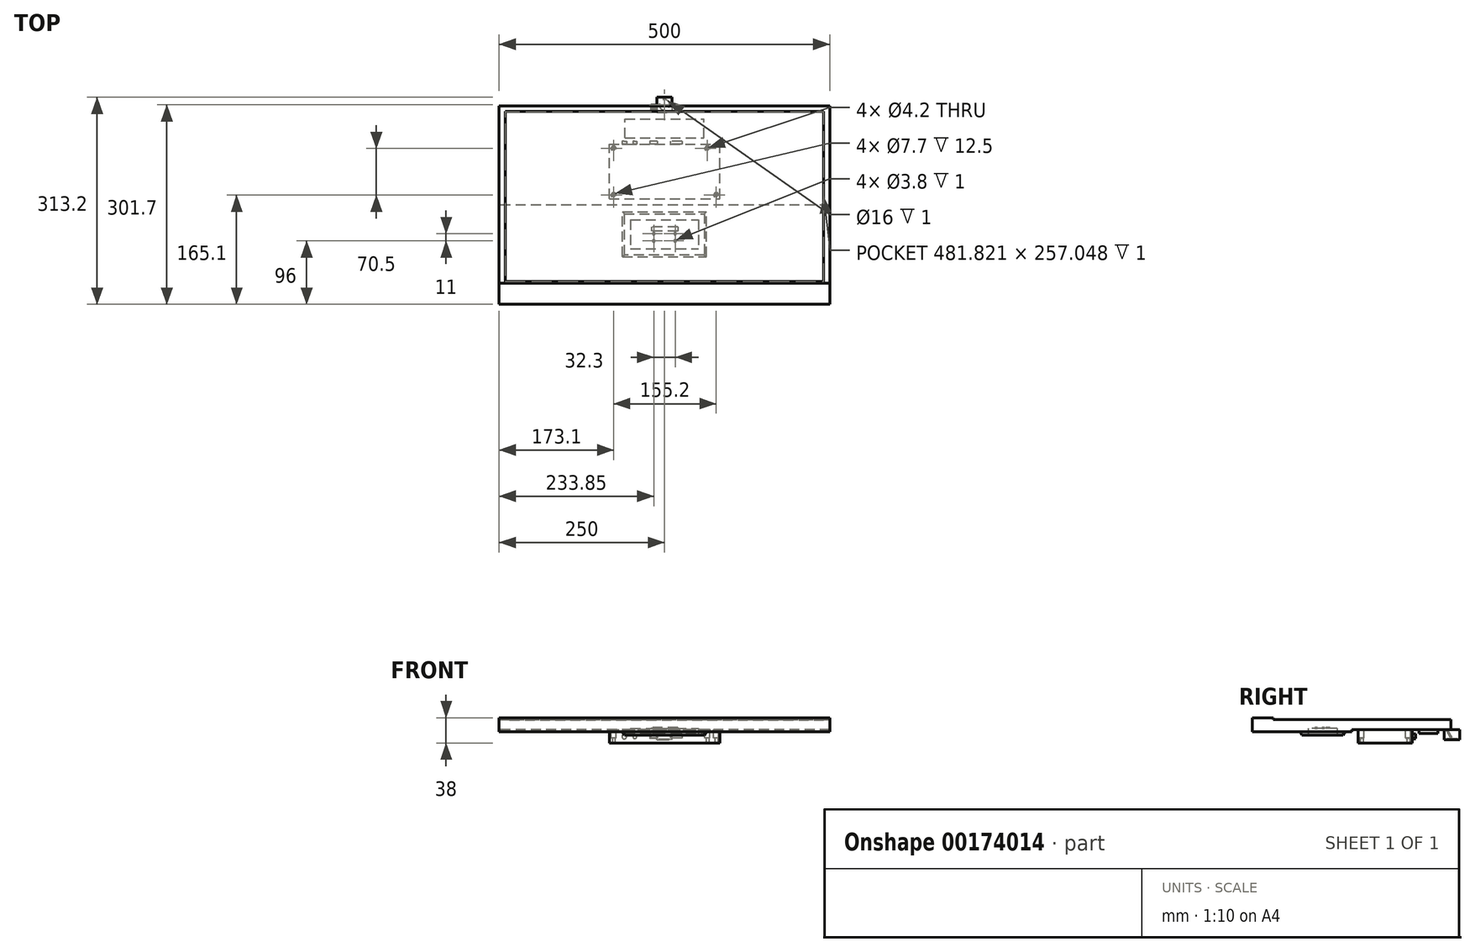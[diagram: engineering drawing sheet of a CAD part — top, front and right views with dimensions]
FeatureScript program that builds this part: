
annotation { "Feature Type Name" : "Feature", "Feature Type Description" : "" }
export const myFeature = defineFeature(function(context is Context, id is Id, definition is map)
    precondition{}
    {
        {
            var Q0;
            Q0=qCreatedBy(makeId("Top.planeOp"),FACE);
            var sketch = newSketch(context, id + "F0", { "sketchPlane" : qUnion([Q0])});
            skLineSegment(sketch, "E0.bottom", {"start": v(250, 150) * mm, "end": v(-250, 150) * mm});
            skLineSegment(sketch, "E0.top", {"start": v(250, -150) * mm, "end": v(-250, -150) * mm});
            skLineSegment(sketch, "E0.left", {"start": v(250, 150) * mm, "end": v(250, -150) * mm});
            skLineSegment(sketch, "E0.right", {"start": v(-250, 150) * mm, "end": v(-250, -150) * mm});
            skPoint(sketch, "E0.middle", {"position": v(0, 0) * mm});
            skSolve(sketch);
        }
        {
            var Q0;
            Q0 = qSketchRegion(id + "F0", true);
            extrude(context, id + "F1", {"entities" : qUnion([Q0]), "depth" : 15 * mm});
        }
        {
            var Q0;
            Q0=makeQuery(id+"F1.opExtrude","CAP_FACE",FACE,{"disambiguationData":[OSD([sQuery(id+"F0.wireOp",EDGE,"E0.bottom"),sQuery(id+"F0.wireOp",EDGE,"E0.top"),sQuery(id+"F0.wireOp",EDGE,"E0.left"),sQuery(id+"F0.wireOp",EDGE,"E0.right")])],"isStart":false});
            var sketch = newSketch(context, id + "F2", { "sketchPlane" : qUnion([Q0])});
            skLineSegment(sketch, "E1.bottom", {"start": v(240.91, 141.46) * mm, "end": v(-240.91, 141.46) * mm});
            skLineSegment(sketch, "E1.top", {"start": v(240.91, -115.59) * mm, "end": v(-240.91, -115.59) * mm});
            skLineSegment(sketch, "E1.left", {"start": v(240.91, 141.46) * mm, "end": v(240.91, -115.59) * mm});
            skLineSegment(sketch, "E1.right", {"start": v(-240.91, 141.46) * mm, "end": v(-240.91, -115.59) * mm});
            skPoint(sketch, "E1.middle", {"position": v(0, 12.94) * mm});
            skSolve(sketch);
        }
        {
            var Q0;
            Q0 = qSketchRegion(id + "F2", true);
            extrude(context, id + "F3", {"entities" : qUnion([Q0]), "operationType" : NewBodyOperationType.REMOVE, "oppositeDirection" : true, "depth" : 1 * mm});
        }
        {
            var Q0;
            Q0=makeQuery(id+"F1.opExtrude","CAP_FACE",FACE,{"disambiguationData":[OSD([sQuery(id+"F0.wireOp",EDGE,"E0.bottom"),sQuery(id+"F0.wireOp",EDGE,"E0.top"),sQuery(id+"F0.wireOp",EDGE,"E0.left"),sQuery(id+"F0.wireOp",EDGE,"E0.right")])],"isStart":true});
            var sketch = newSketch(context, id + "F4", { "sketchPlane" : qUnion([Q0])});
            skLineSegment(sketch, "E2.bottom", {"start": v(250, 150) * mm, "end": v(-250, 150) * mm});
            skLineSegment(sketch, "E2.top", {"start": v(250, 0) * mm, "end": v(-250, 0) * mm});
            skLineSegment(sketch, "E2.left", {"start": v(250, 150) * mm, "end": v(250, 0) * mm});
            skLineSegment(sketch, "E2.right", {"start": v(-250, 150) * mm, "end": v(-250, 0) * mm});
            skSolve(sketch);
        }
        {
            var Q0;
            Q0 = qSketchRegion(id + "F4", true);
            extrude(context, id + "F5", {"entities" : qUnion([Q0]), "operationType" : NewBodyOperationType.ADD, "depth" : 3 * mm});
        }
        {
            var Q0;
            Q0=makeQuery(id+"F5.opExtrude","CAP_FACE",FACE,{"disambiguationData":[OSD([sQuery(id+"F4.wireOp",EDGE,"E2.bottom"),sQuery(id+"F4.wireOp",EDGE,"E2.top"),sQuery(id+"F4.wireOp",EDGE,"E2.left"),sQuery(id+"F4.wireOp",EDGE,"E2.right")])],"isStart":false});
            var sketch = newSketch(context, id + "F6", { "sketchPlane" : qUnion([Q0])});
            skLineSegment(sketch, "E3.bottom", {"start": v(-63.5, 78) * mm, "end": v(63.5, 78) * mm});
            skLineSegment(sketch, "E3.top", {"start": v(-63.5, 10) * mm, "end": v(63.5, 10) * mm});
            skLineSegment(sketch, "E3.left", {"start": v(-63.5, 78) * mm, "end": v(-63.5, 10) * mm});
            skLineSegment(sketch, "E3.right", {"start": v(63.5, 78) * mm, "end": v(63.5, 10) * mm});
            skPoint(sketch, "E3.middle", {"position": v(0, 44) * mm});
            skSolve(sketch);
        }
        {
            var Q0;
            Q0 = qSketchRegion(id + "F6", true);
            extrude(context, id + "F7", {"entities" : qUnion([Q0]), "operationType" : NewBodyOperationType.ADD, "depth" : 5 * mm});
        }
        {
            var Q0;
            Q0=makeQuery(id+"F7.opExtrude","CAP_FACE",FACE,{"disambiguationData":[OSD([sQuery(id+"F6.wireOp",EDGE,"E3.bottom"),sQuery(id+"F6.wireOp",EDGE,"E3.top"),sQuery(id+"F6.wireOp",EDGE,"E3.left"),sQuery(id+"F6.wireOp",EDGE,"E3.right")])],"isStart":false});
            chamfer(context, id + "F8", {"entities" : qUnion([Q0]), "chamferType" : ChamferType.OFFSET_ANGLE, "width" : 5 * mm, "oppositeDirection" : false, "angle" : 30 * degree, "tangentPropagation" : true});
        }
        {
            var Q0;
            Q0=makeQuery(id+"F7.opExtrude","CAP_FACE",FACE,{"disambiguationData":[OSD([sQuery(id+"F6.wireOp",EDGE,"E3.bottom"),sQuery(id+"F6.wireOp",EDGE,"E3.top"),sQuery(id+"F6.wireOp",EDGE,"E3.left"),sQuery(id+"F6.wireOp",EDGE,"E3.right")])],"isStart":false});
            var sketch = newSketch(context, id + "F9", { "sketchPlane" : qUnion([Q0])});
            skLineSegment(sketch, "E4.bottom", {"start": v(-51.3, 22) * mm, "end": v(51.3, 22) * mm});
            skLineSegment(sketch, "E4.top", {"start": v(-51.3, 66) * mm, "end": v(51.3, 66) * mm});
            skLineSegment(sketch, "E4.left", {"start": v(-51.3, 22) * mm, "end": v(-51.3, 66) * mm});
            skLineSegment(sketch, "E4.right", {"start": v(51.3, 22) * mm, "end": v(51.3, 66) * mm});
            skPoint(sketch, "E4.middle", {"position": v(0, 44) * mm});
            skPoint(sketch, "E4.middle.positionSnap0", {"position": v(60.61, 44) * mm});
            skPoint(sketch, "E4.middle.positionSnap1", {"position": v(0, 12.89) * mm});
            skPoint(sketch, "E4.centerSnap0", {"position": v(60.61, 44) * mm});
            skPoint(sketch, "E4.centerSnap1", {"position": v(0, 12.89) * mm});
            skSolve(sketch);
        }
        {
            var Q0;
            Q0 = qSketchRegion(id + "F9", true);
            extrude(context, id + "F10", {"entities" : qUnion([Q0]), "operationType" : NewBodyOperationType.REMOVE, "oppositeDirection" : true, "depth" : 10 * mm});
        }
        {
            var Q0;
            Q0=makeQuery(id+"F1.opExtrude","CAP_FACE",FACE,{"disambiguationData":[OSD([sQuery(id+"F0.wireOp",EDGE,"E0.bottom"),sQuery(id+"F0.wireOp",EDGE,"E0.top"),sQuery(id+"F0.wireOp",EDGE,"E0.left"),sQuery(id+"F0.wireOp",EDGE,"E0.right")])],"isStart":true});
            var sketch = newSketch(context, id + "F11", { "sketchPlane" : qUnion([Q0])});
            skLineSegment(sketch, "E5.bottom", {"start": v(-83.5, -10) * mm, "end": v(83.5, -10) * mm});
            skLineSegment(sketch, "E5.top", {"start": v(-83.5, -92) * mm, "end": v(83.5, -92) * mm});
            skLineSegment(sketch, "E5.left", {"start": v(-83.5, -10) * mm, "end": v(-83.5, -92) * mm});
            skLineSegment(sketch, "E5.right", {"start": v(83.5, -10) * mm, "end": v(83.5, -92) * mm});
            skPoint(sketch, "E5.middle", {"position": v(0, -51) * mm});
            skSolve(sketch);
        }
        {
            var Q0;
            Q0 = qSketchRegion(id + "F11", true);
            extrude(context, id + "F12", {"entities" : qUnion([Q0]), "depth" : 20 * mm});
        }
        {
            var Q0;
            Q0=makeQuery(id+"F12.opExtrude","CAP_FACE",FACE,{"disambiguationData":[OSD([sQuery(id+"F11.wireOp",EDGE,"E5.bottom"),sQuery(id+"F11.wireOp",EDGE,"E5.top"),sQuery(id+"F11.wireOp",EDGE,"E5.left"),sQuery(id+"F11.wireOp",EDGE,"E5.right")])],"isStart":false});
            var sketch = newSketch(context, id + "F13", { "sketchPlane" : qUnion([Q0])});
            skCircle(sketch, "E6", {"center": v(64.9, -85.6) * mm, "radius": 2.1 * mm});
            skCircle(sketch, "E7", {"center": v(78.3, -15.1) * mm, "radius": 2.1 * mm});
            skCircle(sketch, "E8", {"center": v(-76.9, -85.6) * mm, "radius": 2.1 * mm});
            skCircle(sketch, "E9", {"center": v(-76.9, -15.1) * mm, "radius": 2.1 * mm});
            skSolve(sketch);
        }
        {
            var Q0;
            Q0 = qSketchRegion(id + "F13", true);
            extrude(context, id + "F14", {"entities" : qUnion([Q0]), "operationType" : NewBodyOperationType.REMOVE, "endBound" : BoundingType.UP_TO_NEXT, "oppositeDirection" : true, "depth" : 25 * mm});
        }
        {
            var Q0;
            Q0=makeQuery(id+"F12.opExtrude","CAP_FACE",FACE,{"disambiguationData":[OSD([sQuery(id+"F11.wireOp",EDGE,"E5.bottom"),sQuery(id+"F11.wireOp",EDGE,"E5.top"),sQuery(id+"F11.wireOp",EDGE,"E5.left"),sQuery(id+"F11.wireOp",EDGE,"E5.right")])],"isStart":true});
            var sketch = newSketch(context, id + "F15", { "sketchPlane" : qUnion([Q0])});
            skCircle(sketch, "E10", {"center": v(-76.9, 15.1) * mm, "radius": 3.85 * mm});
            skCircle(sketch, "E11", {"center": v(-76.9, 85.6) * mm, "radius": 3.85 * mm});
            skCircle(sketch, "E12", {"center": v(64.9, 85.6) * mm, "radius": 3.85 * mm});
            skCircle(sketch, "E13", {"center": v(78.3, 15.1) * mm, "radius": 3.85 * mm});
            skSolve(sketch);
        }
        {
            var Q0;
            Q0 = qSketchRegion(id + "F15", true);
            extrude(context, id + "F16", {"entities" : qUnion([Q0]), "operationType" : NewBodyOperationType.REMOVE, "oppositeDirection" : true, "depth" : 12.5 * mm});
        }
        {
            var Q0;
            Q0=makeQuery(id+"F12.opExtrude","SWEPT_FACE",FACE,{"disambiguationData":[OSD([sQuery(id+"F11.wireOp",EDGE,"E5.top")])]});
            var sketch = newSketch(context, id + "F17", { "sketchPlane" : qUnion([Q0])});
            skLineSegment(sketch, "E14.bottom", {"start": v(-26.43, -6.48) * mm, "end": v(-8.7, -6.48) * mm});
            skLineSegment(sketch, "E14.top", {"start": v(-26.43, -12.52) * mm, "end": v(-8.7, -12.52) * mm});
            skLineSegment(sketch, "E14.left", {"start": v(-26.43, -6.48) * mm, "end": v(-26.43, -12.52) * mm});
            skLineSegment(sketch, "E14.right", {"start": v(-8.7, -6.48) * mm, "end": v(-8.7, -12.52) * mm});
            skLineSegment(sketch, "E15.bottom", {"start": v(10.66, -7.56) * mm, "end": v(22.37, -7.56) * mm});
            skLineSegment(sketch, "E15.top", {"start": v(10.66, -13.48) * mm, "end": v(22.37, -13.48) * mm});
            skLineSegment(sketch, "E15.left", {"start": v(10.66, -7.56) * mm, "end": v(10.66, -13.48) * mm});
            skLineSegment(sketch, "E15.right", {"start": v(22.37, -7.56) * mm, "end": v(22.37, -13.48) * mm});
            skCircle(sketch, "E16", {"center": v(44.9, -10.33) * mm, "radius": 3.01 * mm});
            skCircle(sketch, "E17", {"center": v(60.8, -10.33) * mm, "radius": 3.56 * mm});
            skSolve(sketch);
        }
        {
            var Q0;
            Q0 = qSketchRegion(id + "F17", true);
            extrude(context, id + "F18", {"entities" : qUnion([Q0]), "operationType" : NewBodyOperationType.ADD, "depth" : 5 * mm});
        }
        {
            var Q0;
            Q0=makeQuery(id+"F1.opExtrude","CAP_FACE",FACE,{"disambiguationData":[OSD([sQuery(id+"F0.wireOp",EDGE,"E0.bottom"),sQuery(id+"F0.wireOp",EDGE,"E0.top"),sQuery(id+"F0.wireOp",EDGE,"E0.left"),sQuery(id+"F0.wireOp",EDGE,"E0.right")])],"isStart":false});
            var sketch = newSketch(context, id + "F19", { "sketchPlane" : qUnion([Q0])});
            skLineSegment(sketch, "E18.bottom", {"start": v(-250, -150) * mm, "end": v(250, -150) * mm});
            skLineSegment(sketch, "E18.top", {"start": v(-250, -118.2) * mm, "end": v(250, -118.2) * mm});
            skLineSegment(sketch, "E18.left", {"start": v(-250, -150) * mm, "end": v(-250, -118.2) * mm});
            skLineSegment(sketch, "E18.right", {"start": v(250, -150) * mm, "end": v(250, -118.2) * mm});
            skSolve(sketch);
        }
        {
            var Q0;
            Q0 = qSketchRegion(id + "F19", true);
            extrude(context, id + "F20", {"entities" : qUnion([Q0]), "operationType" : NewBodyOperationType.ADD, "depth" : 3 * mm});
        }
        {
            var Q0;
            Q0=makeQuery(id+"F10.boolean.opBoolean","COPY",FACE,{"derivedFrom":makeQuery(id+"F10.opExtrude","CAP_FACE",FACE,{"disambiguationData":[OSD([sQuery(id+"F9.wireOp",EDGE,"E4.bottom"),sQuery(id+"F9.wireOp",EDGE,"E4.top"),sQuery(id+"F9.wireOp",EDGE,"E4.left"),sQuery(id+"F9.wireOp",EDGE,"E4.right")])],"isStart":false})});
            var sketch = newSketch(context, id + "F21", { "sketchPlane" : qUnion([Q0])});
            skLineSegment(sketch, "E19.bottom", {"start": v(-16.15, 54) * mm, "end": v(16.15, 54) * mm, "construction": true});
            skLineSegment(sketch, "E19.top", {"start": v(-16.15, 43) * mm, "end": v(16.15, 43) * mm, "construction": true});
            skLineSegment(sketch, "E19.left", {"start": v(-16.15, 54) * mm, "end": v(-16.15, 43) * mm, "construction": true});
            skLineSegment(sketch, "E19.right", {"start": v(16.15, 54) * mm, "end": v(16.15, 43) * mm, "construction": true});
            skPoint(sketch, "E19.middle", {"position": v(0, 48.5) * mm});
            skPoint(sketch, "E19.middle.positionSnap0", {"position": v(0, 22) * mm});
            skPoint(sketch, "E19.centerSnap0", {"position": v(0, 22) * mm});
            skCircle(sketch, "E20", {"center": v(-16.15, 43) * mm, "radius": 1.9 * mm});
            skCircle(sketch, "E21", {"center": v(-16.15, 54) * mm, "radius": 1.9 * mm});
            skCircle(sketch, "E22", {"center": v(16.15, 54) * mm, "radius": 1.9 * mm});
            skCircle(sketch, "E23", {"center": v(16.15, 43) * mm, "radius": 1.9 * mm});
            skLineSegment(sketch, "E24.bottom", {"start": v(20.05, 32.8) * mm, "end": v(-20.05, 32.8) * mm});
            skLineSegment(sketch, "E24.top", {"start": v(20.05, 39.1) * mm, "end": v(-20.05, 39.1) * mm});
            skLineSegment(sketch, "E24.left", {"start": v(20.05, 32.8) * mm, "end": v(20.05, 39.1) * mm});
            skLineSegment(sketch, "E24.right", {"start": v(-20.05, 32.8) * mm, "end": v(-20.05, 39.1) * mm});
            skSolve(sketch);
        }
        {
            var Q0;
            Q0 = qSketchRegion(id + "F21", true);
            extrude(context, id + "F22", {"entities" : qUnion([Q0]), "operationType" : NewBodyOperationType.REMOVE, "oppositeDirection" : true, "depth" : 1 * mm});
        }
        {
            var Q0;
            Q0=makeQuery(id+"F1.opExtrude","CAP_FACE",FACE,{"disambiguationData":[OSD([sQuery(id+"F0.wireOp",EDGE,"E0.bottom"),sQuery(id+"F0.wireOp",EDGE,"E0.top"),sQuery(id+"F0.wireOp",EDGE,"E0.left"),sQuery(id+"F0.wireOp",EDGE,"E0.right")])],"isStart":true});
            var sketch = newSketch(context, id + "F23", { "sketchPlane" : qUnion([Q0])});
            skLineSegment(sketch, "E25.bottom", {"start": v(-59.65, -102) * mm, "end": v(59.65, -102) * mm});
            skLineSegment(sketch, "E25.top", {"start": v(-59.65, -130.2) * mm, "end": v(59.65, -130.2) * mm});
            skLineSegment(sketch, "E25.left", {"start": v(-59.65, -102) * mm, "end": v(-59.65, -130.2) * mm});
            skLineSegment(sketch, "E25.right", {"start": v(59.65, -102) * mm, "end": v(59.65, -130.2) * mm});
            skPoint(sketch, "E25.middle", {"position": v(0, -116.1) * mm});
            skSolve(sketch);
        }
        {
            var Q0;
            Q0 = qSketchRegion(id + "F23", true);
            extrude(context, id + "F24", {"entities" : qUnion([Q0]), "depth" : 5.8 * mm});
        }
        {
            var Q0;
            Q0=makeQuery(id+"F1.opExtrude","CAP_FACE",FACE,{"disambiguationData":[OSD([sQuery(id+"F0.wireOp",EDGE,"E0.bottom"),sQuery(id+"F0.wireOp",EDGE,"E0.top"),sQuery(id+"F0.wireOp",EDGE,"E0.left"),sQuery(id+"F0.wireOp",EDGE,"E0.right")])],"isStart":true});
            var sketch = newSketch(context, id + "F25", { "sketchPlane" : qUnion([Q0])});
            skLineSegment(sketch, "E26.bottom", {"start": v(-11.5, -163.2) * mm, "end": v(11.5, -163.2) * mm});
            skLineSegment(sketch, "E26.top", {"start": v(-11.5, -140.2) * mm, "end": v(11.5, -140.2) * mm});
            skLineSegment(sketch, "E26.left", {"start": v(-11.5, -163.2) * mm, "end": v(-11.5, -140.2) * mm});
            skLineSegment(sketch, "E26.right", {"start": v(11.5, -163.2) * mm, "end": v(11.5, -140.2) * mm});
            skPoint(sketch, "E26.middle", {"position": v(0, -151.7) * mm});
            skSolve(sketch);
        }
        {
            var Q0;
            Q0 = qSketchRegion(id + "F25", true);
            extrude(context, id + "F26", {"entities" : qUnion([Q0]), "depth" : 15 * mm});
        }
        {
            var Q0;
            Q0=makeQuery(id+"F26.opExtrude","SWEPT_FACE",FACE,{"disambiguationData":[OSD([sQuery(id+"F25.wireOp",EDGE,"E26.left")])]});
            var sketch = newSketch(context, id + "F27", { "sketchPlane" : qUnion([Q0])});
            skLineSegment(sketch, "E27", {"start": v(-143.5, -1.5) * mm, "end": v(-145.26, -1.5) * mm});
            skLineSegment(sketch, "E28", {"start": v(-145.26, -1.5) * mm, "end": v(-151.5, -11.7) * mm});
            skLineSegment(sketch, "E29", {"start": v(-151.5, -11.7) * mm, "end": v(-149.74, -11.7) * mm});
            skLineSegment(sketch, "E30", {"start": v(-149.74, -11.7) * mm, "end": v(-143.5, -1.5) * mm});
            skSolve(sketch);
        }
        {
            var Q0;
            Q0 = qSketchRegion(id + "F27", true);
            extrude(context, id + "F28", {"entities" : qUnion([Q0]), "operationType" : NewBodyOperationType.ADD, "depth" : 8.6 * mm});
        }
        {
            var Q0;
            Q0=makeQuery(id+"F28.opExtrude","SWEPT_FACE",FACE,{"disambiguationData":[OSD([sQuery(id+"F27.wireOp",EDGE,"E30")])]});
            var sketch = newSketch(context, id + "F29", { "sketchPlane" : qUnion([Q0])});
            skCircle(sketch, "E31", {"center": v(-15.8, -82.16) * mm, "radius": 2 * mm});
            skPoint(sketch, "E31.centerSnap0", {"position": v(-20.1, -82.16) * mm});
            skPoint(sketch, "E31.centerSnap1", {"position": v(-15.8, -88.14) * mm});
            skSolve(sketch);
        }
        {
            var Q0;
            Q0 = qSketchRegion(id + "F29", true);
            extrude(context, id + "F30", {"entities" : qUnion([Q0]), "operationType" : NewBodyOperationType.REMOVE, "endBound" : BoundingType.UP_TO_NEXT, "oppositeDirection" : true, "depth" : 25 * mm});
        }
        {
            var Q0;
            Q0=makeQuery(id+"F26.opExtrude","CAP_FACE",FACE,{"disambiguationData":[OSD([sQuery(id+"F25.wireOp",EDGE,"E26.bottom"),sQuery(id+"F25.wireOp",EDGE,"E26.top"),sQuery(id+"F25.wireOp",EDGE,"E26.left"),sQuery(id+"F25.wireOp",EDGE,"E26.right")])],"isStart":false});
            var sketch = newSketch(context, id + "F31", { "sketchPlane" : qUnion([Q0])});
            skCircle(sketch, "E32", {"center": v(0, -151.7) * mm, "radius": 8 * mm});
            skPoint(sketch, "E32.centerSnap0", {"position": v(-11.5, -151.7) * mm});
            skPoint(sketch, "E32.centerSnap1", {"position": v(0, -163.2) * mm});
            skSolve(sketch);
        }
        {
            var Q0;
            Q0 = qSketchRegion(id + "F31", true);
            extrude(context, id + "F32", {"entities" : qUnion([Q0]), "operationType" : NewBodyOperationType.REMOVE, "oppositeDirection" : true, "depth" : 1 * mm});
        }
    });
